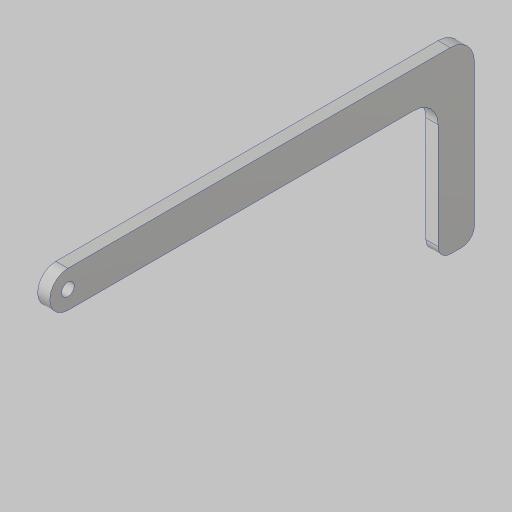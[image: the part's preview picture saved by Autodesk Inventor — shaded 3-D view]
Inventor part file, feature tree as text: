
AUTODESK INVENTOR PART (.ipt)
format: ipt  version: 2023.5 (Build 275446000, 446)  size: 121,856 bytes
history: native  units: in
note: dims shown in document units (in); Inventor stores cm internally (conversion verified against a paired STEP export)
features: sketch x2, fillet x2, extrude x1, hole x1
ambient origin geometry x8: Origin, YZ Plane, XZ Plane, XY Plane, X Axis, Y Axis, Z Axis, Center Point
bodies: Solid1 (feature_tree)
feature tree (6):
  sketch  "Sketch1"  dims[d0=2.0in d1=1.0in d2=0.5in d3=3.38in]
  sketch  "Sketch2"  dims[d4=5.0in d5=3.1875in d6=8.25in d7=23.0in d8=2.0in d9=1.0in d10=0.375in d11=0.375in d12=5.5in d13=0.25in d14=0.0in d15=0.5in d16=0.26in d17=0.266in d18=0.38in d19=0.507in d20=0.25in d21=0.5635in d22=1.0in d23=0.8108in]
  extrude  "Extrusion1"  Depth=0.5in
  fillet  "Fillet1"  Radius=0.5in
  fillet  "Fillet2"  Radius=3.38in
  hole  "Hole1"  [1 undecoded]
note: 1 required parameter value undecoded (feature->parameter linkage not recoverable at this tier; creation-order binding heuristic only, values carry confidence <= 0.55)
